# Revit family: 3722-1Basic
name_source: partatom
category: Doors
units: mm (PartAtom-declared; Revit-internal decimal feet)

## family parameters
Always vertical = Yes
Cut with Voids When Loaded = No
Host = Wall
OmniClass Number = 23.30.10.17.37.14
OmniClass Title = Sectional Overhead Doors
Room Calculation Point = No
Shared = No

## types (1)
- By Type
    Assembly Code = B2030410
    CAD and Specifications = http://www.clopaydoor.com
    Color = White
    Core Material = Expanded polyurethane
    Description = 2'' thick polyurethane insulated, stucco embossed 20 gauge steel flush exterior.
    Door Height = 14' - 0"
    Door Width = 12' - 2"
    Double End Stiles = No
    Exterior Steel = 20 ga. galvanized, primed, and finish painted
    File Revision = 02 (August, 2012)
    FloorToSection2 = 2' - 0"
    FloorToSection3 = 4' - 0"
    FloorToSection4 = 6' - 0"
    FloorToSection5 = 8' - 0"
    FloorToSection6 = 10' - 0"
    FloorToSection7 = 12' - 0"
    Function = Interior
    GreenFormat = http://www.greenformat.com
    Hardware = 14 ga. min. steel hinges; 10-ball steel rollers
    Height = 14' - 0"
    Interior Steel = 28 ga. galvanized, primed, and finish painted
    Keynote = 08 36 13
    LEED = http://products.construction.com
    Manufacturer = Clopay Building Products Company
    Manufacturer Website = http://www.clopaydoor.com
    Maximum Size = Maximum 32' 2'' wide by 26' 0'' high. Additional limitations may apply do to door weight. Consult Clopay for specificiations and shop drawings.
    Model = 3720
    NumArraySections = 2
    NumSections = 7
    NumSectionsNotRounded = 7
    Omniclass Table = 23-30 10 17 37
    Opening Height = 14' - 0"
    Opening Width = 12' - 0"
    Overlap = 0' - 1"
    Overlapping Jamb = Yes
    Product Features and Benefits = http://www.clopaydoor.com
    R-Value = 17.2
    Rough Height = 0' - 0"
    Rough Width = 0' - 0"
    Sales Information = http://www.clopaydoor.com
    Section 3 Glazing = Section : Solid
    Section 4 Glazing = Section : Solid
    Section 5 Glazing = Section : Solid
    Section Height = 2' - 0"
    Spec Wizard = http://www.arcat.com
    Thickness = 0' - 2"
    Track = Galvanized steel (gauge varies according to door size)
    URL = www.clopaydoor.com
    VisArray = Yes
    VisSection3 = Yes
    VisSection4 = Yes
    VisSection5 = Yes
    VisSection6 = No
    Wall Closure = By host
    Width = 12' - 0"
    Windload = Doors available rated for various design pressures; consult Clopay for avaialbility and specifications

## geometry (parser evidence)
native form markers: Sweep x3
no freeform markers — native parametric forms only
